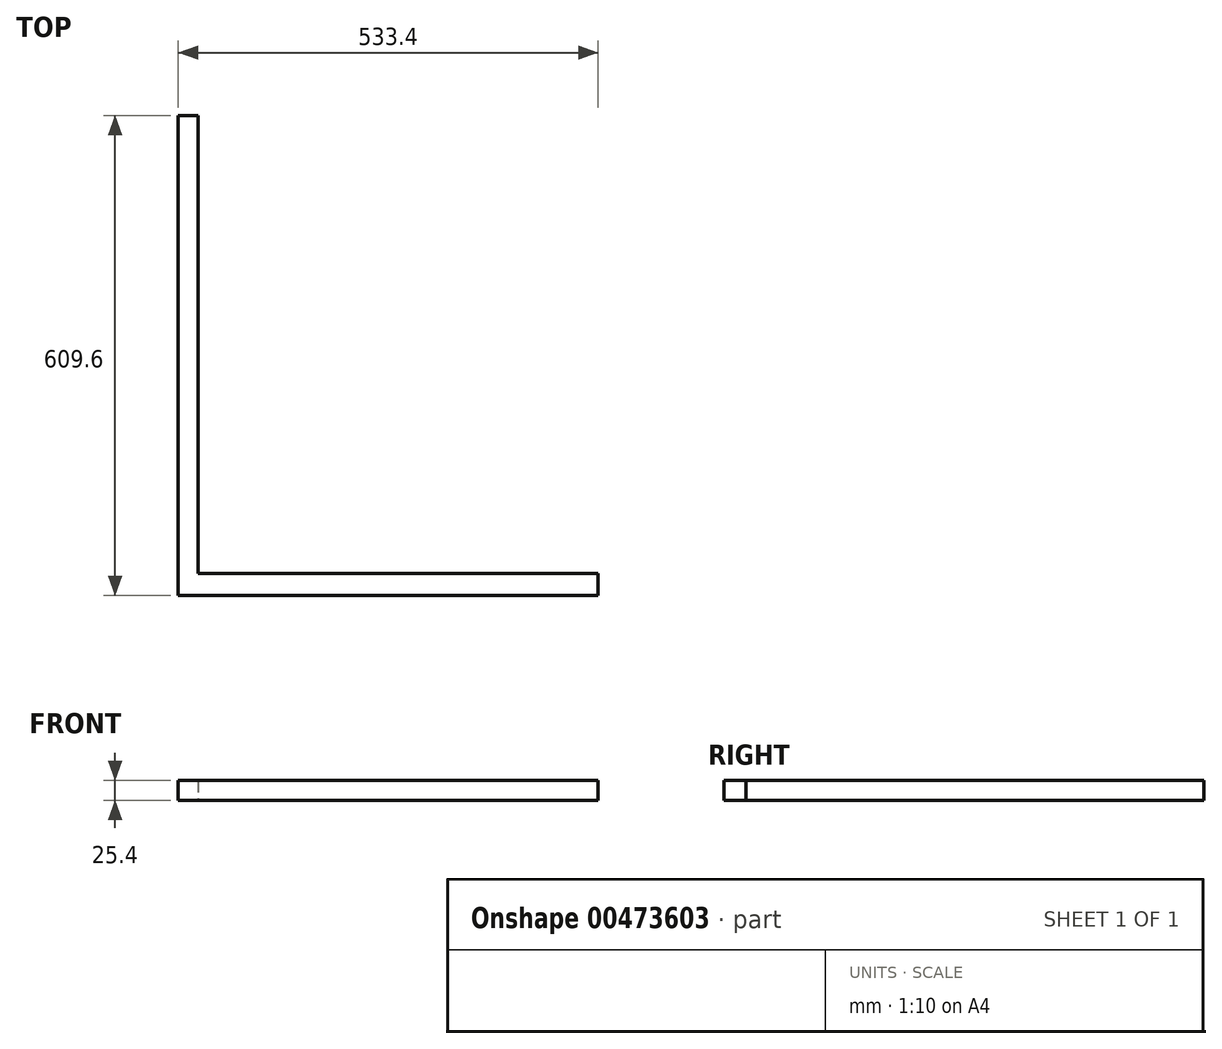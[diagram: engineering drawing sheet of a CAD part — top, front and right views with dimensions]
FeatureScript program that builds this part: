
annotation { "Feature Type Name" : "Feature", "Feature Type Description" : "" }
export const myFeature = defineFeature(function(context is Context, id is Id, definition is map)
    precondition{}
    {
        {
            var Q0;
            Q0=qCreatedBy(makeId("Top.planeOp"),FACE);
            var sketch = newSketch(context, id + "F0", { "sketchPlane" : qUnion([Q0])});
            skLineSegment(sketch, "E0.bottom", {"start": v(-546.1, -304.8) * mm, "end": v(-520.7, -304.8) * mm});
            skLineSegment(sketch, "E0.top", {"start": v(-546.1, 304.8) * mm, "end": v(-520.7, 304.8) * mm});
            skLineSegment(sketch, "E0.left", {"start": v(-546.1, -304.8) * mm, "end": v(-546.1, 304.8) * mm});
            skLineSegment(sketch, "E0.right", {"start": v(-520.7, -304.8) * mm, "end": v(-520.7, 304.8) * mm});
            skPoint(sketch, "E0.middle", {"position": v(-533.4, 0) * mm});
            skLineSegment(sketch, "E1.bottom", {"start": v(12.7, -304.8) * mm, "end": v(-12.7, -304.8) * mm});
            skLineSegment(sketch, "E1.top", {"start": v(12.7, 304.8) * mm, "end": v(-12.7, 304.8) * mm});
            skLineSegment(sketch, "E1.left", {"start": v(12.7, -304.8) * mm, "end": v(12.7, 304.8) * mm});
            skLineSegment(sketch, "E1.right", {"start": v(-12.7, -304.8) * mm, "end": v(-12.7, 304.8) * mm});
            skPoint(sketch, "E1.middle", {"position": v(0, 0) * mm});
            skLineSegment(sketch, "E2.bottom", {"start": v(-546.1, 304.8) * mm, "end": v(12.7, 304.8) * mm});
            skLineSegment(sketch, "E2.top", {"start": v(-546.1, 279.4) * mm, "end": v(12.7, 279.4) * mm});
            skLineSegment(sketch, "E2.left", {"start": v(-546.1, 304.8) * mm, "end": v(-546.1, 279.4) * mm});
            skLineSegment(sketch, "E2.right", {"start": v(12.7, 304.8) * mm, "end": v(12.7, 279.4) * mm});
            skLineSegment(sketch, "E3.bottom", {"start": v(-546.1, -304.8) * mm, "end": v(12.7, -304.8) * mm});
            skLineSegment(sketch, "E3.top", {"start": v(-546.1, -276.76) * mm, "end": v(12.7, -276.76) * mm});
            skLineSegment(sketch, "E3.left", {"start": v(-546.1, -304.8) * mm, "end": v(-546.1, -276.76) * mm});
            skLineSegment(sketch, "E3.right", {"start": v(12.7, -304.8) * mm, "end": v(12.7, -276.76) * mm});
            skSolve(sketch);
        }
        {
            var Q0;
            {var subQ0=sQuery(id+"F0.wireOp",EDGE,"E3.bottom");var subQ1=sQuery(id+"F0.wireOp",EDGE,"E0.right");var subQ2=makeQuery(id+"F0.imprint","INTERSECT",VERTEX,{"derivedFrom":[subQ1,subQ0]});Q0=makeQuery(id+"F0.imprint","IMPRINT",FACE,{"disambiguationData":[TD([[makeQuery(id+"F0.imprint","IMPRINT",EDGE,{"disambiguationData":[TD([[subQ2,-1.0]])],"derivedFrom":subQ1}),-1.0]])]});}
            var Q1;
            {var subQ5=sQuery(id+"F0.wireOp",EDGE,"E3.left");Q1=makeQuery(id+"F0.imprint","IMPRINT",FACE,{"disambiguationData":[TD([[makeQuery(id+"F0.imprint","IMPRINT",EDGE,{"derivedFrom":subQ5}),-1.0]])]});}
            var Q2;
            {var subQ5=sQuery(id+"F0.wireOp",EDGE,"E3.right");Q2=makeQuery(id+"F0.imprint","IMPRINT",FACE,{"disambiguationData":[TD([[makeQuery(id+"F0.imprint","IMPRINT",EDGE,{"derivedFrom":subQ5}),1.0]])]});}
            var Q3;
            {var subQ0=sQuery(id+"F0.wireOp",EDGE,"E0.left");Q3=makeQuery(id+"F0.imprint","IMPRINT",FACE,{"disambiguationData":[TD([[makeQuery(id+"F0.imprint","IMPRINT",EDGE,{"derivedFrom":subQ0}),-1.0]])]});}
            var Q4;
            {var subQ5=sQuery(id+"F0.wireOp",EDGE,"E2.left");Q4=makeQuery(id+"F0.imprint","IMPRINT",FACE,{"disambiguationData":[TD([[makeQuery(id+"F0.imprint","IMPRINT",EDGE,{"derivedFrom":subQ5}),1.0]])]});}
            extrude(context, id + "F1", {"entities" : qUnion([Q0, Q1, Q2, Q3, Q4]), "depth" : 25.4 * mm});
        }
    });
